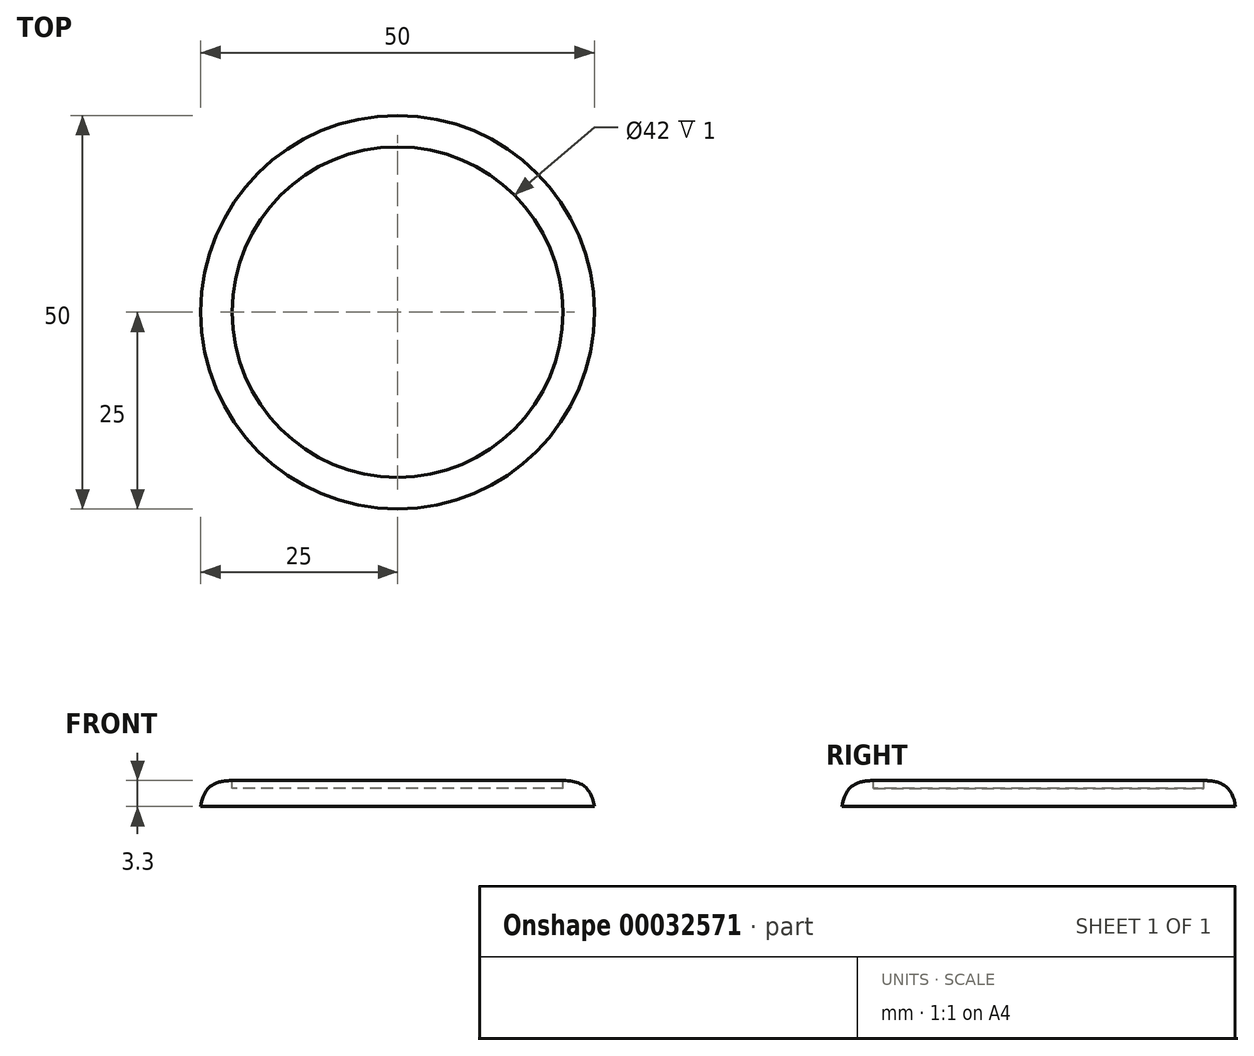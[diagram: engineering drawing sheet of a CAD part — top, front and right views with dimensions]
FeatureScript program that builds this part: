
annotation { "Feature Type Name" : "Feature", "Feature Type Description" : "" }
export const myFeature = defineFeature(function(context is Context, id is Id, definition is map)
    precondition{}
    {
        {
            var Q0;
            Q0=qCreatedBy(makeId("Front.planeOp"),FACE);
            var sketch = newSketch(context, id + "F0", { "sketchPlane" : qUnion([Q0])});
            skLineSegment(sketch, "E0", {"start": v(0, 0) * mm, "end": v(-25, 0) * mm});
            skLineSegment(sketch, "E1", {"start": v(0, 2.3) * mm, "end": v(0, 0) * mm});
            skLineSegment(sketch, "E2", {"start": v(-21, 3.3) * mm, "end": v(-21, 0) * mm, "construction": true});
            skLineSegment(sketch, "E3", {"start": v(-21, 2.3) * mm, "end": v(0, 2.3) * mm});
            skLineSegment(sketch, "E4", {"start": v(-21, 3.3) * mm, "end": v(-21, 2.3) * mm});
            skPoint(sketch, "E5.orphan", {"position": v(0, 3.3) * mm});
            skFitSpline(sketch, "E6", {"points": [v(-21, 3.3) * mm, v(-25, 0) * mm], "startDerivative": vector(-7.96, 0) * mm, "endDerivative": vector(-1.04, -6.6) * mm});
            skSolve(sketch);
        }
        {
            var Q0;
            Q0=qSketchRegion(id+"F0",true);
            var Q1;
            Q1=sQuery(id+"F0.wireOp",EDGE,"E1");
            revolve(context, id + "F1", {"entities" : qUnion([Q0]), "axis" : qUnion([Q1]), "revolveType" : RevolveType.FULL});
        }
    });
